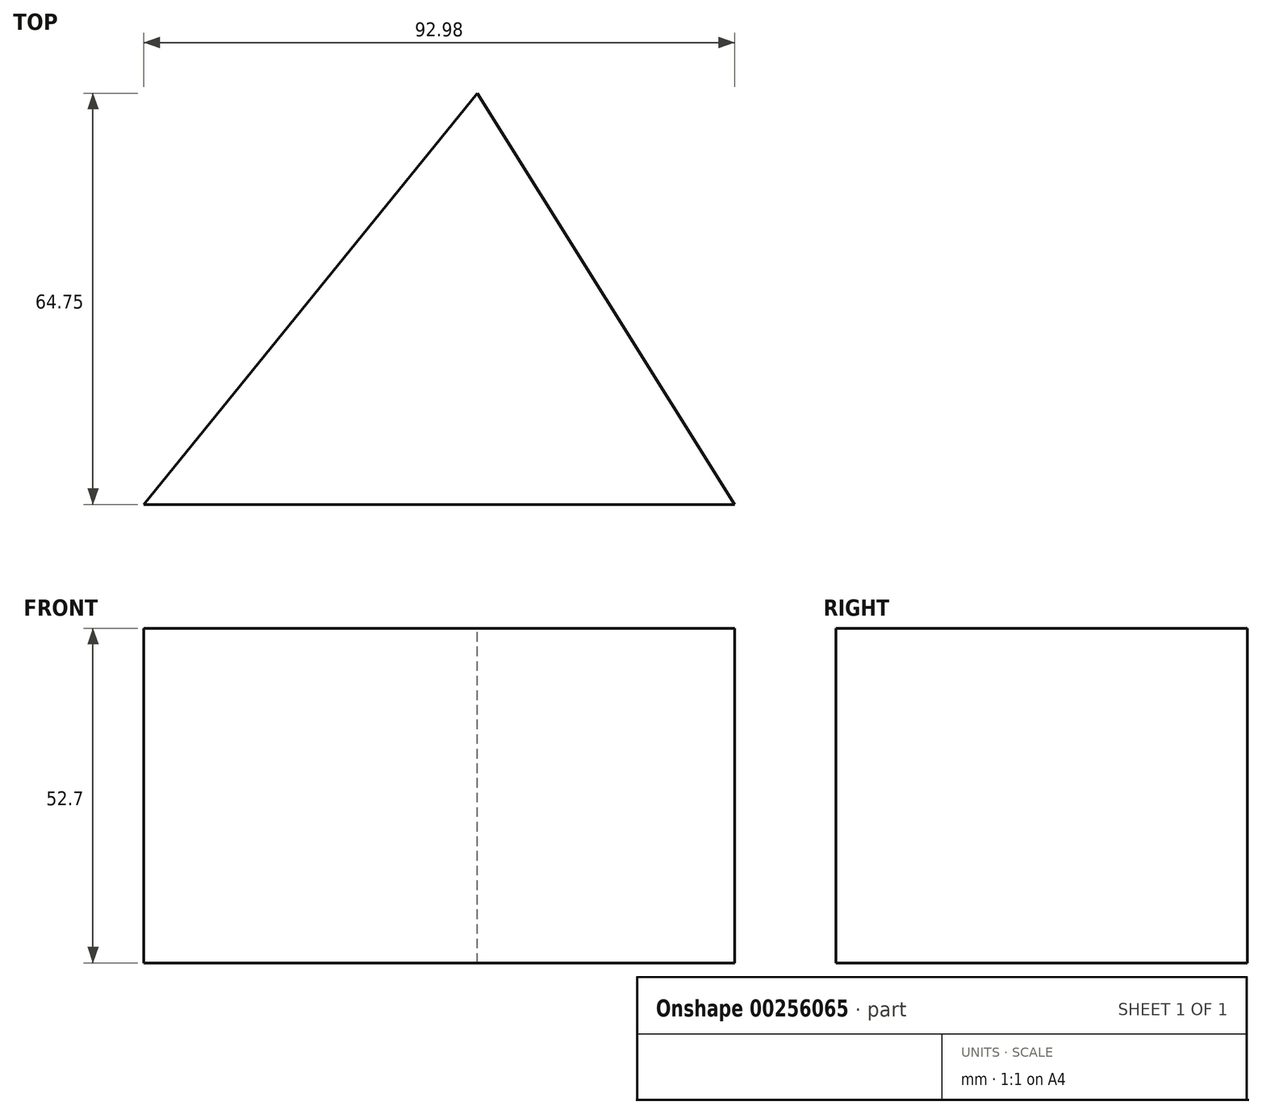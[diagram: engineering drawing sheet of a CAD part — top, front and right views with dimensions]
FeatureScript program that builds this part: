
annotation { "Feature Type Name" : "Feature", "Feature Type Description" : "" }
export const myFeature = defineFeature(function(context is Context, id is Id, definition is map)
    precondition{}
    {
        {
            var Q0;
            Q0=qCreatedBy(makeId("Top.planeOp"),FACE);
            var sketch = newSketch(context, id + "F0", { "sketchPlane" : qUnion([Q0])});
            skLineSegment(sketch, "E0", {"start": v(0, 40.08) * mm, "end": v(-52.48, -24.67) * mm});
            skLineSegment(sketch, "E1", {"start": v(-52.48, -24.67) * mm, "end": v(40.5, -24.67) * mm});
            skLineSegment(sketch, "E2", {"start": v(40.5, -24.67) * mm, "end": v(0, 40.08) * mm});
            skSolve(sketch);
        }
        {
            var Q0;
            Q0=makeQuery(id+"F0.imprint","IMPRINT",FACE,{"disambiguationData":[TD([[makeQuery(id+"F0.imprint","IMPRINT",EDGE,{"derivedFrom":sQuery(id+"F0.wireOp",EDGE,"E0")}),1.0]])]});
            extrude(context, id + "F1", {"entities" : qUnion([Q0]), "oppositeDirection" : true, "depth" : 52.7 * mm});
        }
    });
